# Revit family: Faucet-Lavatory-Grohe-Plus-33170_Series -
name_source: partatom
category: Plumbing Fixtures
revit_build: Autodesk Revit 2018 (Build: 20170223_1515(x64)
units: mm (PartAtom-declared; Revit-internal decimal feet)

## family parameters
Always vertical = No
Cut with Voids When Loaded = No
OmniClass Number = 23.45.55.14
OmniClass Title = Single Faucets
Part Type = Normal
Room Calculation Point = No
Round Connector Dimension = Use Diameter
Shared = Yes
Work Plane-Based = Yes

## types (2) — shared parameters
ADA Compliant = Yes
Assembly Code = D2020300
CW Connection = Yes
CWFU = 1.2
CalGreen Compliant = Yes
Cold Water Connection Diameter = 1/2"
Default Elevation = 0"
Description = PLUS-Single-Handle Bathroom Faucet S-Size
Flow Rate = 1.2 gpm (4.56 L/min)
HW Connection = Yes
HWFU = 1.2
Height = 6 3/4"
Hot Water Connection Diameter = 1"
Installation Type = Deck-Mounted
Length = 4 7/8"
Manufacturer = Grohe
Price = Prices may vary. Please consult Manufacturer Representative for most up-to-date price list.
Product Page URL = https://www.grohe.us
URL = http://www.grohe.us
Vent Connection = No
Warranty Documentation Link = https://cdn.cloud.grohe.com
Waste Connection = No
Width = 2"
cUPC Compliant = Yes
zero-valued in all types: WFU

## per-type parameters (varying)
| type | Finish | Material | Shipping Weight |
| 33170003 | Metal-Grohe-002-Chrome | Metal-Grohe-002-Chrome | 3.87 lb |
| 33170EN3 | Metal-Grohe-EN3-BrushedNickel | Metal-Grohe-EN2-Brushed Nickel | 4.21 lb |

note: column(s) folded — value = type name in every type: Model

## geometry (parser evidence)
native form markers: Sweep x2
no freeform markers — native parametric forms only
